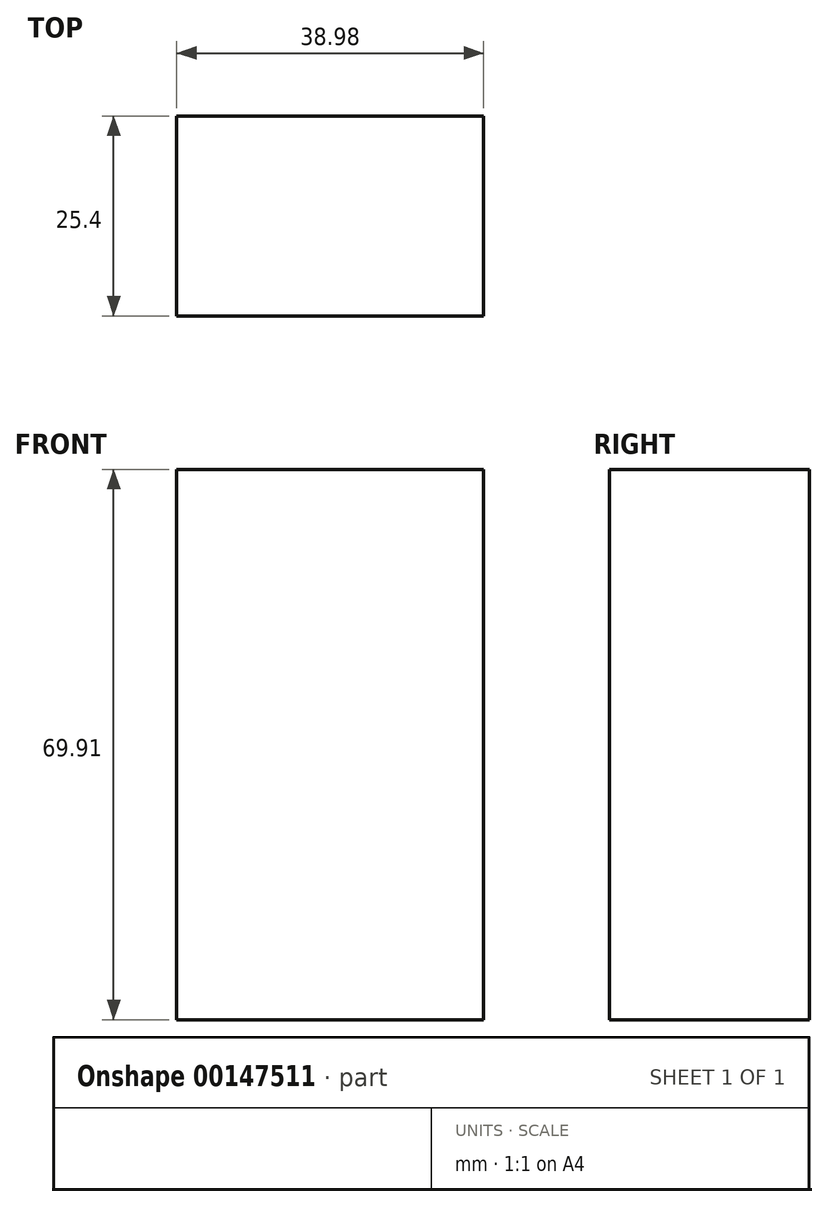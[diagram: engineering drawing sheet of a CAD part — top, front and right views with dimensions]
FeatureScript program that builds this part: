
annotation { "Feature Type Name" : "Feature", "Feature Type Description" : "" }
export const myFeature = defineFeature(function(context is Context, id is Id, definition is map)
    precondition{}
    {
        {
            var Q0;
            Q0=qCreatedBy(makeId("Front.planeOp"),FACE);
            var sketch = newSketch(context, id + "F0", { "sketchPlane" : qUnion([Q0])});
            skLineSegment(sketch, "E0.bottom", {"start": v(-26.94, 29.73) * mm, "end": v(12.04, 29.73) * mm});
            skLineSegment(sketch, "E0.top", {"start": v(-26.94, -40.18) * mm, "end": v(12.04, -40.18) * mm});
            skLineSegment(sketch, "E0.left", {"start": v(-26.94, 29.73) * mm, "end": v(-26.94, -40.18) * mm});
            skLineSegment(sketch, "E0.right", {"start": v(12.04, 29.73) * mm, "end": v(12.04, -40.18) * mm});
            skLineSegment(sketch, "E1", {"start": v(-26.94, 3.1) * mm, "end": v(12.04, 3.1) * mm, "construction": true});
            skLineSegment(sketch, "E2", {"start": v(-26.94, -13.35) * mm, "end": v(12.04, -13.35) * mm, "construction": true});
            skSolve(sketch);
        }
        {
            var Q0;
            Q0 = qSketchRegion(id + "F0", true);
            extrude(context, id + "F1", {"entities" : qUnion([Q0]), "depth" : 25.4 * mm});
        }
    });
